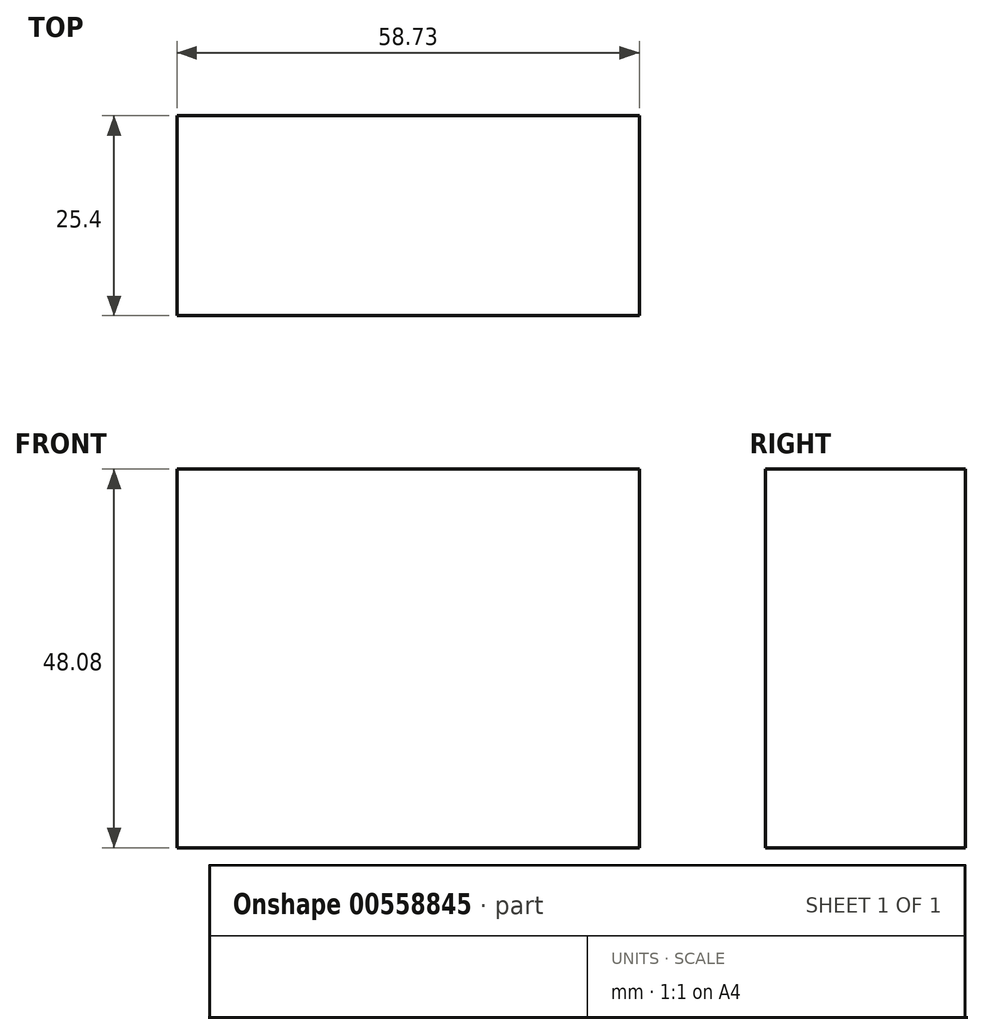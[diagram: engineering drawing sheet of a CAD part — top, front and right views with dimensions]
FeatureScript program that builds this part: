
annotation { "Feature Type Name" : "Feature", "Feature Type Description" : "" }
export const myFeature = defineFeature(function(context is Context, id is Id, definition is map)
    precondition{}
    {
        {
            var Q0;
            Q0=qCreatedBy(makeId("Front.planeOp"),FACE);
            var sketch = newSketch(context, id + "F0", { "sketchPlane" : qUnion([Q0])});
            skLineSegment(sketch, "E0.bottom", {"start": v(-26.8, 24.04) * mm, "end": v(31.93, 24.04) * mm});
            skLineSegment(sketch, "E0.top", {"start": v(-26.8, -24.04) * mm, "end": v(31.93, -24.04) * mm});
            skLineSegment(sketch, "E0.left", {"start": v(-26.8, 24.04) * mm, "end": v(-26.8, -24.04) * mm});
            skLineSegment(sketch, "E0.right", {"start": v(31.93, 24.04) * mm, "end": v(31.93, -24.04) * mm});
            skPoint(sketch, "E0.middle", {"position": v(2.56, 0) * mm});
            skSolve(sketch);
        }
        {
            var Q0;
            Q0=makeQuery(id+"F0.imprint","IMPRINT",FACE,{"disambiguationData":[TD([[makeQuery(id+"F0.imprint","IMPRINT",EDGE,{"derivedFrom":sQuery(id+"F0.wireOp",EDGE,"E0.bottom")}),-1.0]])]});
            extrude(context, id + "F1", {"entities" : qUnion([Q0]), "depth" : 25.4 * mm, "offsetDistance" : 25.4 * mm});
        }
        {
            var Q0;
            Q0=qCreatedBy(makeId("Front.planeOp"),FACE);
            var sketch = newSketch(context, id + "F2", { "sketchPlane" : qUnion([Q0])});
            skCircle(sketch, "E1", {"center": v(0, 0) * mm, "radius": 10.05 * mm});
            skSolve(sketch);
        }
        {
            var Q0;
            Q0 = qSketchRegion(id + "F2", true);
            extrude(context, id + "F3", {"entities" : qUnion([Q0]), "operationType" : NewBodyOperationType.ADD, "depth" : 25.4 * mm, "offsetDistance" : 25.4 * mm});
        }
        {
            var Q0;
            Q0=sQuery(id+"F2.wireOp",EDGE,"E1");
            extrude(context, id + "F4", {"bodyType" : ToolBodyType.SURFACE, "operationType" : NewBodyOperationType.REMOVE, "surfaceEntities" : qUnion([Q0]), "depth" : 50.8 * mm, "offsetDistance" : 25.4 * mm});
        }
    });
